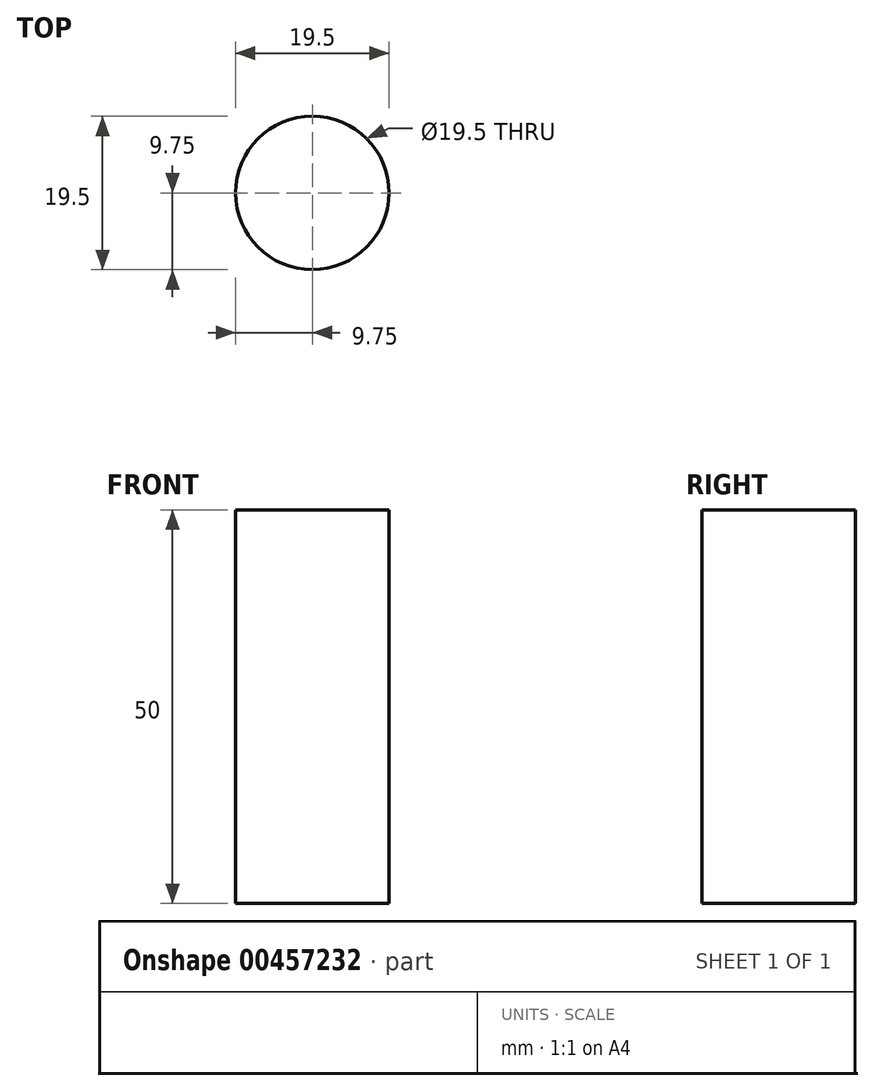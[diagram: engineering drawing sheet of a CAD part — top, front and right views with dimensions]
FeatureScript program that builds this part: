
annotation { "Feature Type Name" : "Feature", "Feature Type Description" : "" }
export const myFeature = defineFeature(function(context is Context, id is Id, definition is map)
    precondition{}
    {
        {
            var Q0;
            Q0=qCreatedBy(makeId("Front.planeOp"),FACE);
            var sketch = newSketch(context, id + "F0", { "sketchPlane" : qUnion([Q0])});
            skLineSegment(sketch, "E0.bottom", {"start": v(-9.75, 2.25) * mm, "end": v(9.75, 2.25) * mm});
            skLineSegment(sketch, "E0.top", {"start": v(-9.75, -2.25) * mm, "end": v(9.75, -2.25) * mm});
            skLineSegment(sketch, "E0.left", {"start": v(-9.75, 2.25) * mm, "end": v(-9.75, -2.25) * mm});
            skLineSegment(sketch, "E0.right", {"start": v(9.75, 2.25) * mm, "end": v(9.75, -2.25) * mm});
            skPoint(sketch, "E0.middle", {"position": v(0, 0) * mm});
            skSolve(sketch);
        }
        {
            var Q0;
            Q0=qCreatedBy(makeId("Front.planeOp"),FACE);
            var sketch = newSketch(context, id + "F1", { "sketchPlane" : qUnion([Q0])});
            skLineSegment(sketch, "E1.bottom", {"start": v(-9.76, -2.1) * mm, "end": v(9.76, -2.1) * mm});
            skLineSegment(sketch, "E1.top", {"start": v(-9.76, -50.88) * mm, "end": v(9.76, -50.88) * mm});
            skLineSegment(sketch, "E1.left", {"start": v(-9.76, -2.1) * mm, "end": v(-9.76, -50.88) * mm});
            skLineSegment(sketch, "E1.right", {"start": v(9.76, -2.1) * mm, "end": v(9.76, -50.88) * mm});
            skPoint(sketch, "E1.middle", {"position": v(0, -26.5) * mm});
            skSolve(sketch);
        }
        {
            var Q0;
            Q0=qCreatedBy(makeId("Front.planeOp"),FACE);
            var sketch = newSketch(context, id + "F2", { "sketchPlane" : qUnion([Q0])});
            skCircle(sketch, "E2.cCircle", {"center": v(0, -56.58) * mm, "radius": 5.63 * mm, "construction": true});
            skLineSegment(sketch, "E2.0", {"start": v(-9.76, -50.95) * mm, "end": v(9.76, -50.95) * mm});
            skLineSegment(sketch, "E2.1", {"start": v(9.76, -50.95) * mm, "end": v(0, -67.85) * mm});
            skLineSegment(sketch, "E2.2", {"start": v(0, -67.85) * mm, "end": v(-9.76, -50.95) * mm});
            skPoint(sketch, "E2.0.midPoint", {"position": v(0, -50.95) * mm});
            skSolve(sketch);
        }
        {
            var Q0;
            Q0=qCreatedBy(makeId("Front.planeOp"),FACE);
            var sketch = newSketch(context, id + "F3", { "sketchPlane" : qUnion([Q0])});
            skLineSegment(sketch, "E3.bottom", {"start": v(-9.75, 52.38) * mm, "end": v(9.75, 52.38) * mm});
            skLineSegment(sketch, "E3.top", {"start": v(-9.75, 2.38) * mm, "end": v(9.75, 2.38) * mm});
            skLineSegment(sketch, "E3.left", {"start": v(-9.75, 52.38) * mm, "end": v(-9.75, 2.38) * mm});
            skLineSegment(sketch, "E3.right", {"start": v(9.75, 52.38) * mm, "end": v(9.75, 2.38) * mm});
            skPoint(sketch, "E3.middle", {"position": v(0, 27.38) * mm});
            skSolve(sketch);
        }
        {
            var Q0;
            Q0=qCreatedBy(makeId("Front.planeOp"),FACE);
            var sketch = newSketch(context, id + "F4", { "sketchPlane" : qUnion([Q0])});
            skLineSegment(sketch, "E4", {"start": v(0, 75.1) * mm, "end": v(0, -91.25) * mm});
            skSolve(sketch);
        }
        {
            var Q0;
            Q0 = qSketchRegion(id + "F3", true);
            var Q1;
            Q1=sQuery(id+"F3.wireOp",EDGE,"E3.left");
            var Q2;
            Q2=sQuery(id+"F4.wireOp",EDGE,"E4");
            revolve(context, id + "F5", {"bodyType" : ToolBodyType.SURFACE, "entities" : qUnion([Q0]), "surfaceEntities" : qUnion([Q1]), "axis" : qUnion([Q2]), "revolveType" : RevolveType.FULL});
        }
    });
